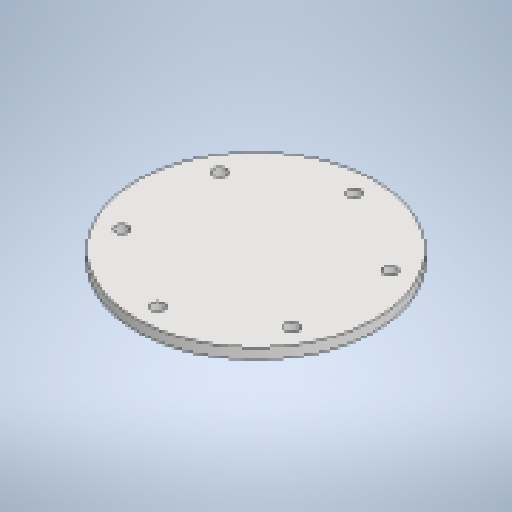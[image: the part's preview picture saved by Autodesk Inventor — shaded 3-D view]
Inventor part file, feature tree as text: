
AUTODESK INVENTOR PART (.ipt)
format: ipt  version: 2025 (Build 290162010, 162A)  size: 193,536 bytes
history: native  units: mm
features: sketch x2, other x2, sheet_metal_op x1, extrude x1, pattern_circular x1
ambient origin geometry x8: Origin, YZ Plane, XZ Plane, XY Plane, X Axis, Y Axis, Z Axis, Center Point
bodies: Body1 (feature_tree)
feature tree (7):
  sheet_metal_op  "Face1"
  extrude  "Extrusion6"  Depth=10.0mm
  pattern_circular  "Circular Pattern3"  [2 undecoded]
  sketch  "Sketch6"  dims[d45=10.0mm d46=145.0mm]
  other  "Plate1"
  sketch  "Sketch8"  dims[d47=225.0mm d50=12.0mm d51=185.0mm d52=3.5mm d53=0.0mm d54=60.0mm d55=360.0deg]
  other  "Definition1"
note: 2 required parameter values undecoded (feature->parameter linkage not recoverable at this tier; creation-order binding heuristic only, values carry confidence <= 0.55)
